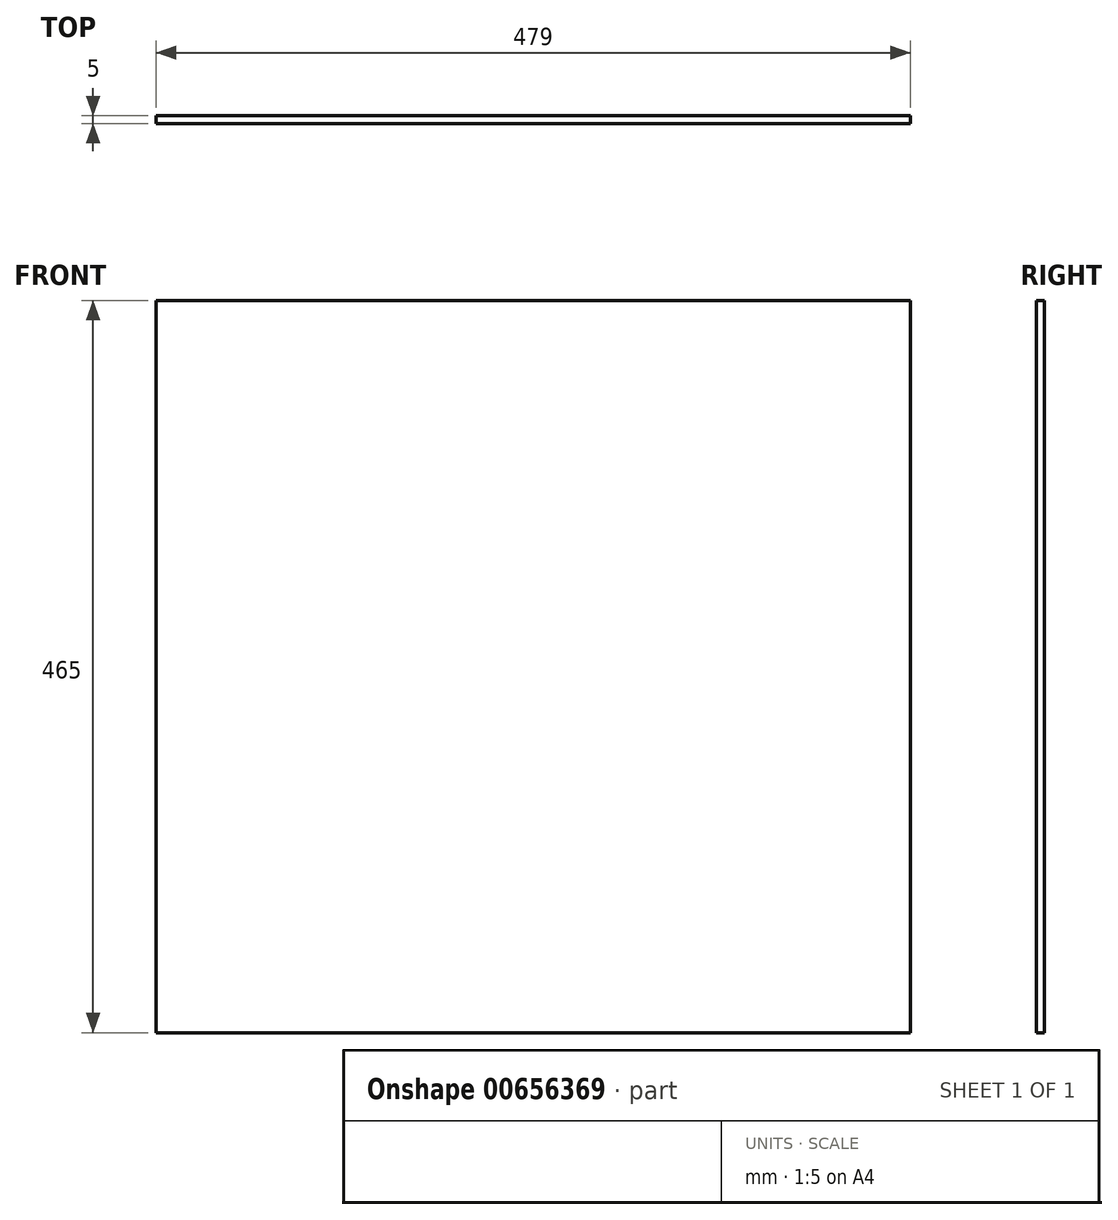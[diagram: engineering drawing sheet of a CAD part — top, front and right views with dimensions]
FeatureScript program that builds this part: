
annotation { "Feature Type Name" : "Feature", "Feature Type Description" : "" }
export const myFeature = defineFeature(function(context is Context, id is Id, definition is map)
    precondition{}
    {
        {
            var Q0;
            Q0=qCreatedBy(makeId("Top.planeOp"),FACE);
            var sketch = newSketch(context, id + "F0", { "sketchPlane" : qUnion([Q0])});
            skLineSegment(sketch, "E0.bottom", {"start": v(0, 0) * mm, "end": v(479, 0) * mm});
            skLineSegment(sketch, "E0.top", {"start": v(0, 5) * mm, "end": v(479, 5) * mm});
            skLineSegment(sketch, "E0.left", {"start": v(0, 0) * mm, "end": v(0, 5) * mm});
            skLineSegment(sketch, "E0.right", {"start": v(479, 0) * mm, "end": v(479, 5) * mm});
            skSolve(sketch);
        }
        {
            var Q0;
            Q0=makeQuery(id+"F0.imprint","IMPRINT",FACE,{"disambiguationData":[TD([[makeQuery(id+"F0.imprint","IMPRINT",EDGE,{"derivedFrom":sQuery(id+"F0.wireOp",EDGE,"E0.bottom")}),1.0]])]});
            extrude(context, id + "F1", {"entities" : qUnion([Q0]), "depth" : 465 * mm, "offsetDistance" : 25 * mm});
        }
    });
